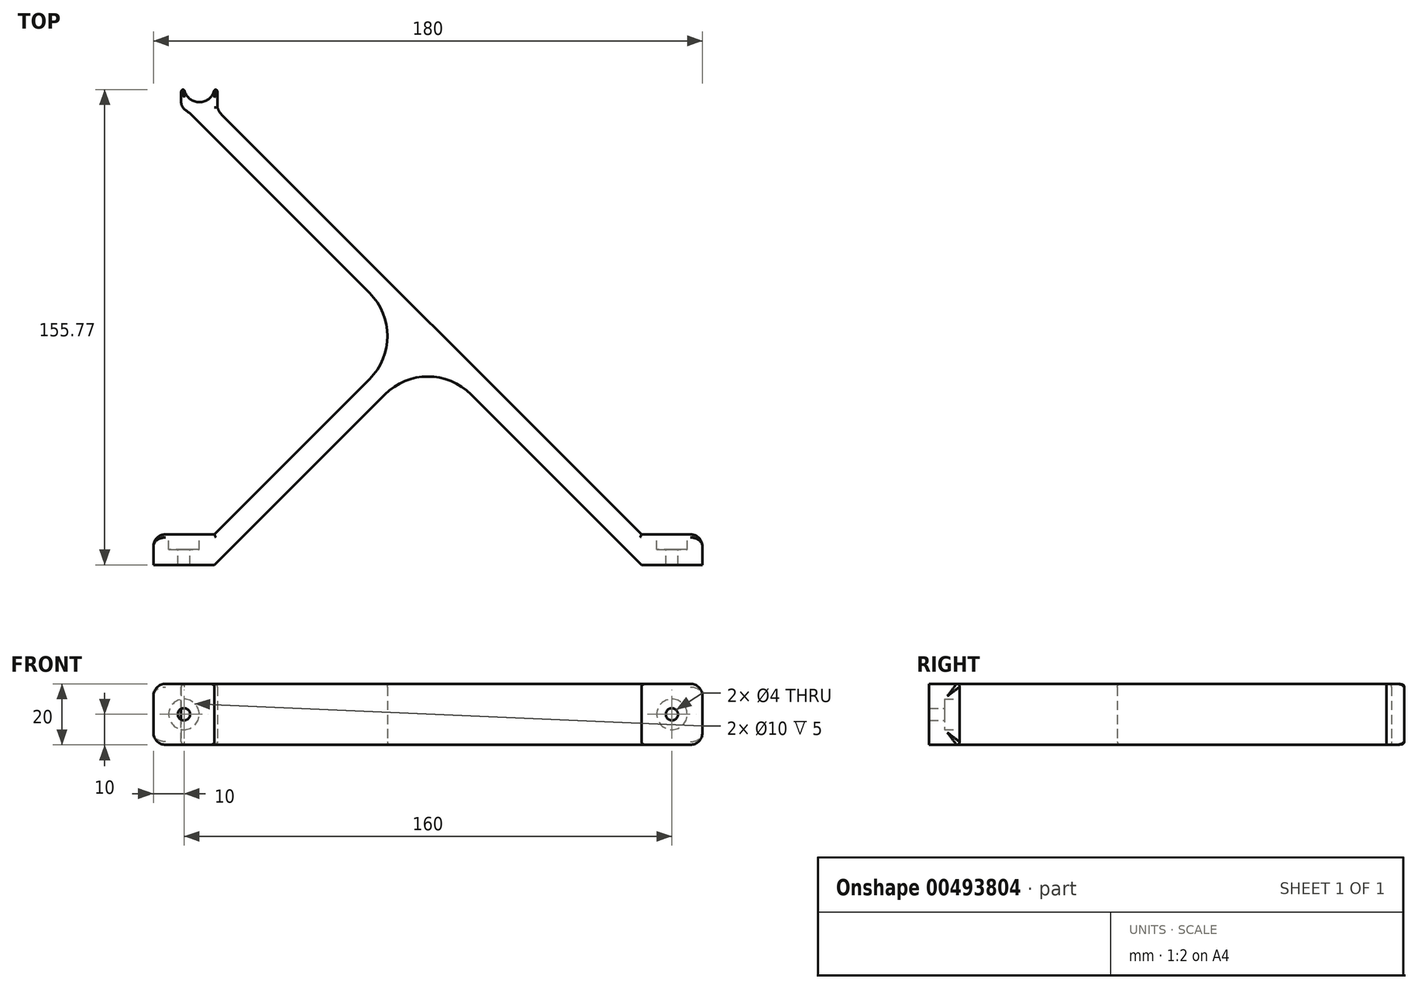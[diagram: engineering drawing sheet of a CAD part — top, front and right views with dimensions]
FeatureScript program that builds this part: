
annotation { "Feature Type Name" : "Feature", "Feature Type Description" : "" }
export const myFeature = defineFeature(function(context is Context, id is Id, definition is map)
    precondition{}
    {
        {
            var Q0;
            Q0=qCreatedBy(makeId("Top.planeOp"),FACE);
            var sketch = newSketch(context, id + "F0", { "sketchPlane" : qUnion([Q0])});
            skLineSegment(sketch, "E0", {"start": v(0, 0) * mm, "end": v(0, -75) * mm, "construction": true});
            skLineSegment(sketch, "E1", {"start": v(0, -75) * mm, "end": v(75, -75) * mm, "construction": true});
            skLineSegment(sketch, "E2", {"start": v(75, -75) * mm, "end": v(-74.9, 74.9) * mm});
            skLineSegment(sketch, "E3", {"start": v(0, 0) * mm, "end": v(-75, -75) * mm});
            skLineSegment(sketch, "E4", {"start": v(-147, -24.26) * mm, "end": v(-137, -24.26) * mm});
            skPoint(sketch, "E5", {"position": v(-142, -24.26) * mm});
            skLineSegment(sketch, "E6", {"start": v(-80, -75) * mm, "end": v(-70, -75) * mm});
            skPoint(sketch, "E7", {"position": v(-75, -75) * mm});
            skLineSegment(sketch, "E8", {"start": v(70, -75) * mm, "end": v(80, -75) * mm});
            skPoint(sketch, "E9", {"position": v(75, -75) * mm});
            skLineSegment(sketch, "E10", {"start": v(-5, -5) * mm, "end": v(5, -5) * mm});
            skPoint(sketch, "E11", {"position": v(0, -5) * mm});
            skLineSegment(sketch, "E12", {"start": v(-70, -75) * mm, "end": v(0, -5) * mm});
            skLineSegment(sketch, "E13", {"start": v(0, -5) * mm, "end": v(70, -75) * mm});
            skLineSegment(sketch, "E14", {"start": v(-5, 5) * mm, "end": v(-5, -5) * mm});
            skPoint(sketch, "E15", {"position": v(-5, 0) * mm});
            skLineSegment(sketch, "E16", {"start": v(-80, -75) * mm, "end": v(-5, 0) * mm});
            skLineSegment(sketch, "E17", {"start": v(80, -75) * mm, "end": v(-70, 75) * mm});
            skLineSegment(sketch, "E18", {"start": v(-70, 75) * mm, "end": v(-74.9, 74.9) * mm});
            skLineSegment(sketch, "E19", {"start": v(-74.9, 74.9) * mm, "end": v(-79.9, 74.9) * mm});
            skLineSegment(sketch, "E20", {"start": v(-79.9, 74.9) * mm, "end": v(-5, 0) * mm});
            skLineSegment(sketch, "E21", {"start": v(-5, 0) * mm, "end": v(-19.14, 14.14) * mm, "construction": true});
            skLineSegment(sketch, "E22", {"start": v(-5, 0) * mm, "end": v(-19.14, -14.14) * mm, "construction": true});
            skArc(sketch, "E23", {"start": v(-19.14, -14.14) * mm, "mid": v(-13.28, 0) * mm, "end": v(-19.14, 14.14) * mm});
            skLineSegment(sketch, "E24", {"start": v(0, -5) * mm, "end": v(-14.14, -19.14) * mm, "construction": true});
            skLineSegment(sketch, "E25", {"start": v(0, -5) * mm, "end": v(14.14, -19.14) * mm, "construction": true});
            skArc(sketch, "E26", {"start": v(14.14, -19.14) * mm, "mid": v(0, -13.28) * mm, "end": v(-14.14, -19.14) * mm});
            skLineSegment(sketch, "E27.bottom", {"start": v(-70, -75) * mm, "end": v(-90, -75) * mm});
            skLineSegment(sketch, "E27.top", {"start": v(-70, -65) * mm, "end": v(-90, -65) * mm});
            skLineSegment(sketch, "E27.left", {"start": v(-70, -75) * mm, "end": v(-70, -65) * mm});
            skLineSegment(sketch, "E27.right", {"start": v(-90, -75) * mm, "end": v(-90, -65) * mm});
            skLineSegment(sketch, "E28.bottom", {"start": v(70, -75) * mm, "end": v(90, -75) * mm});
            skLineSegment(sketch, "E28.top", {"start": v(70, -65) * mm, "end": v(90, -65) * mm});
            skLineSegment(sketch, "E28.left", {"start": v(70, -75) * mm, "end": v(70, -65) * mm});
            skLineSegment(sketch, "E28.right", {"start": v(90, -75) * mm, "end": v(90, -65) * mm});
            skArc(sketch, "E29", {"start": v(-79.9, 80.98) * mm, "mid": v(-74.95, 76.66) * mm, "end": v(-70, 80.98) * mm});
            skLineSegment(sketch, "E30", {"start": v(-79.9, 80.98) * mm, "end": v(-79.9, 74.9) * mm});
            skLineSegment(sketch, "E31", {"start": v(-70, 80.98) * mm, "end": v(-70, 75) * mm});
            skLineSegment(sketch, "E32", {"start": v(-79.9, 74.9) * mm, "end": v(-80.9, 74.9) * mm});
            skLineSegment(sketch, "E33", {"start": v(-80.9, 74.9) * mm, "end": v(-80.9, 80.98) * mm});
            skLineSegment(sketch, "E34", {"start": v(-79.9, 80.98) * mm, "end": v(-80.9, 80.98) * mm});
            skLineSegment(sketch, "E35", {"start": v(-70, 75) * mm, "end": v(-69, 75) * mm});
            skLineSegment(sketch, "E36", {"start": v(-69, 75) * mm, "end": v(-69, 80.98) * mm});
            skLineSegment(sketch, "E37", {"start": v(-69, 80.98) * mm, "end": v(-70, 80.98) * mm});
            skSolve(sketch);
        }
        {
            var Q0;
            {var subQ5=sQuery(id+"F0.wireOp",EDGE,"E12");Q0=makeQuery(id+"F0.imprint","IMPRINT",FACE,{"disambiguationData":[TD([[makeQuery(id+"F0.imprint","IMPRINT",EDGE,{"derivedFrom":subQ5}),1.0]])]});}
            var Q1;
            {var subQ5=sQuery(id+"F0.wireOp",EDGE,"E16");Q1=makeQuery(id+"F0.imprint","IMPRINT",FACE,{"disambiguationData":[TD([[makeQuery(id+"F0.imprint","IMPRINT",EDGE,{"derivedFrom":subQ5}),-1.0]])]});}
            var Q2;
            {var subQ5=sQuery(id+"F0.wireOp",EDGE,"E13");Q2=makeQuery(id+"F0.imprint","IMPRINT",FACE,{"disambiguationData":[TD([[makeQuery(id+"F0.imprint","IMPRINT",EDGE,{"derivedFrom":subQ5}),1.0]])]});}
            var Q3;
            {var subQ7=sQuery(id+"F0.wireOp",EDGE,"E17");Q3=makeQuery(id+"F0.imprint","IMPRINT",FACE,{"disambiguationData":[TD([[makeQuery(id+"F0.imprint","IMPRINT",EDGE,{"derivedFrom":subQ7}),1.0]])]});}
            var Q4;
            {var subQ0=sQuery(id+"F0.wireOp",EDGE,"E19");Q4=makeQuery(id+"F0.imprint","IMPRINT",FACE,{"disambiguationData":[TD([[makeQuery(id+"F0.imprint","IMPRINT",EDGE,{"derivedFrom":subQ0}),1.0]])]});}
            var Q5;
            {var subQ0=sQuery(id+"F0.wireOp",EDGE,"E3");var subQ1=sQuery(id+"F0.wireOp",EDGE,"E2");var subQ2=makeQuery(id+"F0.imprint","INTERSECT",VERTEX,{"derivedFrom":[subQ1,subQ0]});Q5=makeQuery(id+"F0.imprint","IMPRINT",FACE,{"disambiguationData":[TD([[makeQuery(id+"F0.imprint","IMPRINT",EDGE,{"disambiguationData":[TD([[subQ2,-1.0]])],"derivedFrom":subQ1}),1.0]])]});}
            var Q6;
            {var subQ0=sQuery(id+"F0.wireOp",EDGE,"E3");var subQ1=sQuery(id+"F0.wireOp",EDGE,"E2");var subQ2=makeQuery(id+"F0.imprint","INTERSECT",VERTEX,{"derivedFrom":[subQ1,subQ0]});Q6=makeQuery(id+"F0.imprint","IMPRINT",FACE,{"disambiguationData":[TD([[makeQuery(id+"F0.imprint","IMPRINT",EDGE,{"disambiguationData":[TD([[subQ2,1.0]])],"derivedFrom":subQ1}),1.0]])]});}
            var Q7;
            {var subQ3=sQuery(id+"F0.wireOp",EDGE,"E26");Q7=makeQuery(id+"F0.imprint","IMPRINT",FACE,{"disambiguationData":[TD([[makeQuery(id+"F0.imprint","IMPRINT",EDGE,{"derivedFrom":subQ3}),-1.0]])]});}
            var Q8;
            {var subQ3=sQuery(id+"F0.wireOp",EDGE,"E23");Q8=makeQuery(id+"F0.imprint","IMPRINT",FACE,{"disambiguationData":[TD([[makeQuery(id+"F0.imprint","IMPRINT",EDGE,{"derivedFrom":subQ3}),-1.0]])]});}
            var Q9;
            {var subQ3=sQuery(id+"F0.wireOp",EDGE,"E28.top");Q9=makeQuery(id+"F0.imprint","IMPRINT",FACE,{"disambiguationData":[TD([[makeQuery(id+"F0.imprint","IMPRINT",EDGE,{"derivedFrom":subQ3}),-1.0]])]});}
            var Q10;
            {var subQ0=sQuery(id+"F0.wireOp",EDGE,"E28.bottom");var subQ1=sQuery(id+"F0.wireOp",EDGE,"E2");var subQ2=makeQuery(id+"F0.imprint","INTERSECT",VERTEX,{"derivedFrom":[subQ1,subQ0]});Q10=makeQuery(id+"F0.imprint","IMPRINT",FACE,{"disambiguationData":[TD([[makeQuery(id+"F0.imprint","IMPRINT",EDGE,{"disambiguationData":[TD([[subQ2,-1.0]])],"derivedFrom":subQ1}),1.0]])]});}
            var Q11;
            {var subQ0=sQuery(id+"F0.wireOp",EDGE,"E18");Q11=makeQuery(id+"F0.imprint","IMPRINT",FACE,{"disambiguationData":[TD([[makeQuery(id+"F0.imprint","IMPRINT",EDGE,{"derivedFrom":subQ0}),1.0]])]});}
            var Q12;
            {var subQ0=sQuery(id+"F0.wireOp",EDGE,"E27.bottom");var subQ1=sQuery(id+"F0.wireOp",EDGE,"E3");var subQ2=makeQuery(id+"F0.imprint","INTERSECT",VERTEX,{"derivedFrom":[subQ1,subQ0]});Q12=makeQuery(id+"F0.imprint","IMPRINT",FACE,{"disambiguationData":[TD([[makeQuery(id+"F0.imprint","IMPRINT",EDGE,{"disambiguationData":[TD([[subQ2,1.0]])],"derivedFrom":subQ1}),-1.0]])]});}
            var Q13;
            {var subQ0=sQuery(id+"F0.wireOp",EDGE,"E27.bottom");var subQ1=sQuery(id+"F0.wireOp",EDGE,"E3");var subQ2=makeQuery(id+"F0.imprint","INTERSECT",VERTEX,{"derivedFrom":[subQ1,subQ0]});Q13=makeQuery(id+"F0.imprint","IMPRINT",FACE,{"disambiguationData":[TD([[makeQuery(id+"F0.imprint","IMPRINT",EDGE,{"disambiguationData":[TD([[subQ2,1.0]])],"derivedFrom":subQ1}),1.0]])]});}
            var Q14;
            {var subQ3=sQuery(id+"F0.wireOp",EDGE,"E27.top");Q14=makeQuery(id+"F0.imprint","IMPRINT",FACE,{"disambiguationData":[TD([[makeQuery(id+"F0.imprint","IMPRINT",EDGE,{"derivedFrom":subQ3}),1.0]])]});}
            var Q15;
            Q15=makeQuery(id+"F0.imprint","IMPRINT",FACE,{"disambiguationData":[TD([[makeQuery(id+"F0.imprint","IMPRINT",EDGE,{"derivedFrom":sQuery(id+"F0.wireOp",EDGE,"E18")}),-1.0]])]});
            var Q16;
            Q16=makeQuery(id+"F0.imprint","IMPRINT",FACE,{"disambiguationData":[TD([[makeQuery(id+"F0.imprint","IMPRINT",EDGE,{"derivedFrom":sQuery(id+"F0.wireOp",EDGE,"E30")}),-1.0]])]});
            var Q17;
            Q17=makeQuery(id+"F0.imprint","IMPRINT",FACE,{"disambiguationData":[TD([[makeQuery(id+"F0.imprint","IMPRINT",EDGE,{"derivedFrom":sQuery(id+"F0.wireOp",EDGE,"E31")}),1.0]])]});
            extrude(context, id + "F1", {"entities" : qUnion([Q0, Q1, Q2, Q3, Q4, Q5, Q6, Q7, Q8, Q9, Q10, Q11, Q12, Q13, Q14, Q15, Q16, Q17]), "endBound" : BoundingType.SYMMETRIC, "depth" : 20 * mm});
        }
        {
            var Q0;
            Q0=makeQuery(id+"F1.opExtrude","SWEPT_EDGE",EDGE,{"disambiguationData":[OSD([sQuery(id+"F0.wireOp",EDGE,"E19"),sQuery(id+"F0.wireOp",EDGE,"E20"),sQuery(id+"F0.wireOp",EDGE,"E30"),sQuery(id+"F0.wireOp",EDGE,"E32")])]});
            fillet(context, id + "F2", {"entities" : qUnion([Q0]), "radius" : 15 * mm, "tangentPropagation" : true, "allowEdgeOverflow" : false});
        }
        {
            var Q0;
            Q0=makeQuery(id+"F1.opExtrude","SWEPT_EDGE",EDGE,{"disambiguationData":[OSD([sQuery(id+"F0.wireOp",EDGE,"E17"),sQuery(id+"F0.wireOp",EDGE,"E18"),sQuery(id+"F0.wireOp",EDGE,"E31"),sQuery(id+"F0.wireOp",EDGE,"E35")])]});
            fillet(context, id + "F3", {"entities" : qUnion([Q0]), "radius" : 5 * mm, "tangentPropagation" : true, "allowEdgeOverflow" : false});
        }
        {
            var Q0;
            Q0=makeQuery(id+"F2.opFillet","BLEND_EDGE",EDGE,{"blendedFrom":[makeQuery(id+"F1.opExtrude","SWEPT_EDGE",EDGE,{"disambiguationData":[OSD([sQuery(id+"F0.wireOp",EDGE,"E19"),sQuery(id+"F0.wireOp",EDGE,"E20"),sQuery(id+"F0.wireOp",EDGE,"E30"),sQuery(id+"F0.wireOp",EDGE,"E32")])]}),makeQuery(id+"F1.opExtrude","SWEPT_FACE",FACE,{"disambiguationData":[OSD([sQuery(id+"F0.wireOp",EDGE,"E33")])]})],"blendedInto":[makeQuery(id+"F1.opExtrude","SWEPT_FACE",FACE,{"disambiguationData":[OSD([sQuery(id+"F0.wireOp",EDGE,"E33")])]})]});
            fillet(context, id + "F4", {"entities" : qUnion([Q0]), "radius" : 3 * mm, "tangentPropagation" : true, "allowEdgeOverflow" : false});
        }
        {
            var Q0;
            Q0=makeQuery(id+"F1.opExtrude","SWEPT_FACE",FACE,{"disambiguationData":[OSD([sQuery(id+"F0.wireOp",EDGE,"E27.top")])]});
            var sketch = newSketch(context, id + "F5", { "sketchPlane" : qUnion([Q0])});
            skPoint(sketch, "E38", {"position": v(80, 0) * mm});
            skPoint(sketch, "E38.positionSnap0", {"position": v(80, -10) * mm});
            skPoint(sketch, "E38.positionSnap1", {"position": v(90, 0) * mm});
            skCircle(sketch, "E39", {"center": v(80, 0) * mm, "radius": 5 * mm});
            skCircle(sketch, "E40", {"center": v(80, 0) * mm, "radius": 2 * mm});
            skSolve(sketch);
        }
        {
            var Q0;
            Q0=makeQuery(id+"F1.opExtrude","SWEPT_FACE",FACE,{"disambiguationData":[OSD([sQuery(id+"F0.wireOp",EDGE,"E28.top")])]});
            var sketch = newSketch(context, id + "F6", { "sketchPlane" : qUnion([Q0])});
            skPoint(sketch, "E41", {"position": v(-80, 0) * mm});
            skPoint(sketch, "E41.positionSnap0", {"position": v(-80, 10) * mm});
            skPoint(sketch, "E41.positionSnap1", {"position": v(-70, 0) * mm});
            skPoint(sketch, "E42.positionSnap0", {"position": v(-80, -8.37) * mm});
            skPoint(sketch, "E42.positionSnap1", {"position": v(-77.63, 0) * mm});
            skCircle(sketch, "E43", {"center": v(-80, 0) * mm, "radius": 5 * mm});
            skCircle(sketch, "E44", {"center": v(-80, 0) * mm, "radius": 2 * mm});
            skSolve(sketch);
        }
        {
            var Q0;
            Q0=makeQuery(id+"F5.imprint","IMPRINT",FACE,{"disambiguationData":[TD([[makeQuery(id+"F5.imprint","IMPRINT",EDGE,{"derivedFrom":sQuery(id+"F5.wireOp",EDGE,"E40")}),1.0]])]});
            var Q1;
            Q1=makeQuery(id+"F6.imprint","IMPRINT",FACE,{"disambiguationData":[TD([[makeQuery(id+"F6.imprint","IMPRINT",EDGE,{"derivedFrom":sQuery(id+"F6.wireOp",EDGE,"E44")}),1.0]])]});
            extrude(context, id + "F7", {"entities" : qUnion([Q0, Q1]), "operationType" : NewBodyOperationType.REMOVE, "oppositeDirection" : true, "depth" : 25 * mm});
        }
        {
            var Q0;
            Q0=makeQuery(id+"F5.imprint","IMPRINT",FACE,{"disambiguationData":[TD([[makeQuery(id+"F5.imprint","IMPRINT",EDGE,{"derivedFrom":sQuery(id+"F5.wireOp",EDGE,"E39")}),1.0]])]});
            var Q1;
            Q1 = qSketchRegion(id + "F6", true);
            extrude(context, id + "F8", {"entities" : qUnion([Q0, Q1]), "operationType" : NewBodyOperationType.REMOVE, "oppositeDirection" : true, "depth" : 5 * mm});
        }
        {
            var Q0;
            Q0=makeQuery(id+"F1.opExtrude","SWEPT_EDGE",EDGE,{"disambiguationData":[OSD([sQuery(id+"F0.wireOp",EDGE,"E27.top"),sQuery(id+"F0.wireOp",EDGE,"E27.right")])]});
            var Q1;
            Q1=makeQuery(id+"F1.opExtrude","CAP_EDGE",EDGE,{"disambiguationData":[OSD([sQuery(id+"F0.wireOp",EDGE,"E27.right")])],"isStart":false});
            var Q2;
            Q2=makeQuery(id+"F1.opExtrude","CAP_EDGE",EDGE,{"disambiguationData":[OSD([sQuery(id+"F0.wireOp",EDGE,"E27.right")])],"isStart":true});
            var Q3;
            Q3=makeQuery(id+"F1.opExtrude","CAP_EDGE",EDGE,{"disambiguationData":[OSD([sQuery(id+"F0.wireOp",EDGE,"E28.right")])],"isStart":false});
            var Q4;
            Q4=makeQuery(id+"F1.opExtrude","CAP_EDGE",EDGE,{"disambiguationData":[OSD([sQuery(id+"F0.wireOp",EDGE,"E28.right")])],"isStart":true});
            var Q5;
            Q5=makeQuery(id+"F1.opExtrude","SWEPT_EDGE",EDGE,{"disambiguationData":[OSD([sQuery(id+"F0.wireOp",EDGE,"E28.top"),sQuery(id+"F0.wireOp",EDGE,"E28.right")])]});
            fillet(context, id + "F9", {"entities" : qUnion([Q0, Q1, Q2, Q3, Q4, Q5]), "radius" : 4 * mm, "tangentPropagation" : true, "allowEdgeOverflow" : false});
        }
        {
            var Q0;
            Q0=makeQuery(id+"F1.opExtrude","CAP_EDGE",EDGE,{"disambiguationData":[OSD([sQuery(id+"F0.wireOp",EDGE,"E28.top")])],"isStart":true});
            var Q1;
            Q1=makeQuery(id+"F1.opExtrude","CAP_EDGE",EDGE,{"disambiguationData":[OSD([sQuery(id+"F0.wireOp",EDGE,"E28.top")])],"isStart":false});
            var Q2;
            Q2=makeQuery(id+"F1.opExtrude","CAP_EDGE",EDGE,{"disambiguationData":[OSD([sQuery(id+"F0.wireOp",EDGE,"E17")])],"isStart":true});
            var Q3;
            Q3=makeQuery(id+"F1.opExtrude","CAP_EDGE",EDGE,{"disambiguationData":[OSD([sQuery(id+"F0.wireOp",EDGE,"E17")])],"isStart":false});
            var Q4;
            Q4=makeQuery(id+"F1.opExtrude","CAP_EDGE",EDGE,{"disambiguationData":[OSD([sQuery(id+"F0.wireOp",EDGE,"E27.top")])],"isStart":true});
            var Q5;
            Q5=makeQuery(id+"F1.opExtrude","CAP_EDGE",EDGE,{"disambiguationData":[OSD([sQuery(id+"F0.wireOp",EDGE,"E27.top")])],"isStart":false});
            var Q6;
            Q6=makeQuery(id+"F1.opExtrude","CAP_EDGE",EDGE,{"disambiguationData":[OSD([sQuery(id+"F0.wireOp",EDGE,"E13")])],"isStart":true});
            var Q7;
            Q7=makeQuery(id+"F1.opExtrude","CAP_EDGE",EDGE,{"disambiguationData":[OSD([sQuery(id+"F0.wireOp",EDGE,"E13")])],"isStart":false});
            fillet(context, id + "F10", {"entities" : qUnion([Q0, Q1, Q2, Q3, Q4, Q5, Q6, Q7]), "radius" : 1 * mm, "tangentPropagation" : true, "allowEdgeOverflow" : false});
        }
        {
            var Q0;
            Q0=makeQuery(id+"F1.opExtrude","SWEPT_EDGE",EDGE,{"disambiguationData":[OSD([sQuery(id+"F0.wireOp",EDGE,"E29"),sQuery(id+"F0.wireOp",EDGE,"E31"),sQuery(id+"F0.wireOp",EDGE,"E37")])]});
            var Q1;
            Q1=makeQuery(id+"F1.opExtrude","SWEPT_EDGE",EDGE,{"disambiguationData":[OSD([sQuery(id+"F0.wireOp",EDGE,"E36"),sQuery(id+"F0.wireOp",EDGE,"E37")])]});
            var Q2;
            Q2=makeQuery(id+"F1.opExtrude","SWEPT_EDGE",EDGE,{"disambiguationData":[OSD([sQuery(id+"F0.wireOp",EDGE,"E29"),sQuery(id+"F0.wireOp",EDGE,"E30"),sQuery(id+"F0.wireOp",EDGE,"E34")])]});
            var Q3;
            Q3=makeQuery(id+"F1.opExtrude","SWEPT_EDGE",EDGE,{"disambiguationData":[OSD([sQuery(id+"F0.wireOp",EDGE,"E33"),sQuery(id+"F0.wireOp",EDGE,"E34")])]});
            fillet(context, id + "F11", {"entities" : qUnion([Q0, Q1, Q2, Q3]), "radius" : 1 * mm, "tangentPropagation" : true, "allowEdgeOverflow" : false});
        }
        {
            var Q0;
            {var subQ0=sQuery(id+"F0.wireOp",EDGE,"E37");Q0=makeQuery(id+"F11.opFillet","BLEND_EDGE",EDGE,{"blendedFrom":[makeQuery(id+"F1.opExtrude","SWEPT_EDGE",EDGE,{"disambiguationData":[OSD([sQuery(id+"F0.wireOp",EDGE,"E29"),sQuery(id+"F0.wireOp",EDGE,"E31"),subQ0])]}),makeQuery(id+"F1.opExtrude","SWEPT_EDGE",EDGE,{"disambiguationData":[OSD([sQuery(id+"F0.wireOp",EDGE,"E36"),subQ0])]})],"blendedInto":[]});}
            var Q1;
            {var subQ0=sQuery(id+"F0.wireOp",EDGE,"E34");Q1=makeQuery(id+"F11.opFillet","BLEND_EDGE",EDGE,{"blendedFrom":[makeQuery(id+"F1.opExtrude","SWEPT_EDGE",EDGE,{"disambiguationData":[OSD([sQuery(id+"F0.wireOp",EDGE,"E29"),sQuery(id+"F0.wireOp",EDGE,"E30"),subQ0])]}),makeQuery(id+"F1.opExtrude","SWEPT_EDGE",EDGE,{"disambiguationData":[OSD([sQuery(id+"F0.wireOp",EDGE,"E33"),subQ0])]})],"blendedInto":[]});}
            fillet(context, id + "F12", {"entities" : qUnion([Q0, Q1]), "radius" : .5 * mm, "tangentPropagation" : true, "allowEdgeOverflow" : false});
        }
        {
            var Q0;
            Q0=makeQuery(id+"F1.opExtrude","CAP_EDGE",EDGE,{"disambiguationData":[OSD([sQuery(id+"F0.wireOp",EDGE,"E36")])],"isStart":true});
            var Q1;
            Q1=makeQuery(id+"F1.opExtrude","CAP_EDGE",EDGE,{"disambiguationData":[OSD([sQuery(id+"F0.wireOp",EDGE,"E36")])],"isStart":false});
            var Q2;
            Q2=makeQuery(id+"F1.opExtrude","CAP_EDGE",EDGE,{"disambiguationData":[OSD([sQuery(id+"F0.wireOp",EDGE,"E33")])],"isStart":true});
            var Q3;
            {var subQ0=sQuery(id+"F0.wireOp",EDGE,"E33");var subQ1=sQuery(id+"F0.wireOp",EDGE,"E32");var subQ2=sQuery(id+"F0.wireOp",EDGE,"E20");Q3=makeQuery(id+"F4.opFillet","BLEND_EDGE",EDGE,{"blendedFrom":[makeQuery(id+"F2.opFillet","BLEND_EDGE",EDGE,{"blendedFrom":[makeQuery(id+"F1.opExtrude","SWEPT_EDGE",EDGE,{"disambiguationData":[OSD([sQuery(id+"F0.wireOp",EDGE,"E19"),subQ2,sQuery(id+"F0.wireOp",EDGE,"E30"),subQ1])]}),makeQuery(id+"F1.opExtrude","SWEPT_FACE",FACE,{"disambiguationData":[OSD([subQ0])]})],"blendedInto":[makeQuery(id+"F1.opExtrude","SWEPT_FACE",FACE,{"disambiguationData":[OSD([subQ0])]})]}),makeQuery(id+"F1.opExtrude","CAP_FACE",FACE,{"disambiguationData":[OSD([sQuery(id+"F0.wireOp",EDGE,"E12"),sQuery(id+"F0.wireOp",EDGE,"E13"),sQuery(id+"F0.wireOp",EDGE,"E16"),sQuery(id+"F0.wireOp",EDGE,"E17"),subQ2,sQuery(id+"F0.wireOp",EDGE,"E23"),sQuery(id+"F0.wireOp",EDGE,"E26"),sQuery(id+"F0.wireOp",EDGE,"E27.bottom"),sQuery(id+"F0.wireOp",EDGE,"E27.top"),sQuery(id+"F0.wireOp",EDGE,"E27.right"),sQuery(id+"F0.wireOp",EDGE,"E28.bottom"),sQuery(id+"F0.wireOp",EDGE,"E28.top"),sQuery(id+"F0.wireOp",EDGE,"E28.right"),sQuery(id+"F0.wireOp",EDGE,"E29"),subQ1,subQ0,sQuery(id+"F0.wireOp",EDGE,"E34"),sQuery(id+"F0.wireOp",EDGE,"E35"),sQuery(id+"F0.wireOp",EDGE,"E36"),sQuery(id+"F0.wireOp",EDGE,"E37")])],"isStart":true})],"blendedInto":[makeQuery(id+"F1.opExtrude","CAP_FACE",FACE,{"disambiguationData":[OSD([sQuery(id+"F0.wireOp",EDGE,"E12"),sQuery(id+"F0.wireOp",EDGE,"E13"),sQuery(id+"F0.wireOp",EDGE,"E16"),sQuery(id+"F0.wireOp",EDGE,"E17"),subQ2,sQuery(id+"F0.wireOp",EDGE,"E23"),sQuery(id+"F0.wireOp",EDGE,"E26"),sQuery(id+"F0.wireOp",EDGE,"E27.bottom"),sQuery(id+"F0.wireOp",EDGE,"E27.top"),sQuery(id+"F0.wireOp",EDGE,"E27.right"),sQuery(id+"F0.wireOp",EDGE,"E28.bottom"),sQuery(id+"F0.wireOp",EDGE,"E28.top"),sQuery(id+"F0.wireOp",EDGE,"E28.right"),sQuery(id+"F0.wireOp",EDGE,"E29"),subQ1,subQ0,sQuery(id+"F0.wireOp",EDGE,"E34"),sQuery(id+"F0.wireOp",EDGE,"E35"),sQuery(id+"F0.wireOp",EDGE,"E36"),sQuery(id+"F0.wireOp",EDGE,"E37")])],"isStart":true})]});}
            var Q4;
            Q4=makeQuery(id+"F1.opExtrude","CAP_EDGE",EDGE,{"disambiguationData":[OSD([sQuery(id+"F0.wireOp",EDGE,"E33")])],"isStart":false});
            var Q5;
            {var subQ0=sQuery(id+"F0.wireOp",EDGE,"E33");var subQ1=sQuery(id+"F0.wireOp",EDGE,"E32");var subQ2=sQuery(id+"F0.wireOp",EDGE,"E20");Q5=makeQuery(id+"F4.opFillet","BLEND_EDGE",EDGE,{"blendedFrom":[makeQuery(id+"F2.opFillet","BLEND_EDGE",EDGE,{"blendedFrom":[makeQuery(id+"F1.opExtrude","SWEPT_EDGE",EDGE,{"disambiguationData":[OSD([sQuery(id+"F0.wireOp",EDGE,"E19"),subQ2,sQuery(id+"F0.wireOp",EDGE,"E30"),subQ1])]}),makeQuery(id+"F1.opExtrude","SWEPT_FACE",FACE,{"disambiguationData":[OSD([subQ0])]})],"blendedInto":[makeQuery(id+"F1.opExtrude","SWEPT_FACE",FACE,{"disambiguationData":[OSD([subQ0])]})]}),makeQuery(id+"F1.opExtrude","CAP_FACE",FACE,{"disambiguationData":[OSD([sQuery(id+"F0.wireOp",EDGE,"E12"),sQuery(id+"F0.wireOp",EDGE,"E13"),sQuery(id+"F0.wireOp",EDGE,"E16"),sQuery(id+"F0.wireOp",EDGE,"E17"),subQ2,sQuery(id+"F0.wireOp",EDGE,"E23"),sQuery(id+"F0.wireOp",EDGE,"E26"),sQuery(id+"F0.wireOp",EDGE,"E27.bottom"),sQuery(id+"F0.wireOp",EDGE,"E27.top"),sQuery(id+"F0.wireOp",EDGE,"E27.right"),sQuery(id+"F0.wireOp",EDGE,"E28.bottom"),sQuery(id+"F0.wireOp",EDGE,"E28.top"),sQuery(id+"F0.wireOp",EDGE,"E28.right"),sQuery(id+"F0.wireOp",EDGE,"E29"),subQ1,subQ0,sQuery(id+"F0.wireOp",EDGE,"E34"),sQuery(id+"F0.wireOp",EDGE,"E35"),sQuery(id+"F0.wireOp",EDGE,"E36"),sQuery(id+"F0.wireOp",EDGE,"E37")])],"isStart":false})],"blendedInto":[makeQuery(id+"F1.opExtrude","CAP_FACE",FACE,{"disambiguationData":[OSD([sQuery(id+"F0.wireOp",EDGE,"E12"),sQuery(id+"F0.wireOp",EDGE,"E13"),sQuery(id+"F0.wireOp",EDGE,"E16"),sQuery(id+"F0.wireOp",EDGE,"E17"),subQ2,sQuery(id+"F0.wireOp",EDGE,"E23"),sQuery(id+"F0.wireOp",EDGE,"E26"),sQuery(id+"F0.wireOp",EDGE,"E27.bottom"),sQuery(id+"F0.wireOp",EDGE,"E27.top"),sQuery(id+"F0.wireOp",EDGE,"E27.right"),sQuery(id+"F0.wireOp",EDGE,"E28.bottom"),sQuery(id+"F0.wireOp",EDGE,"E28.top"),sQuery(id+"F0.wireOp",EDGE,"E28.right"),sQuery(id+"F0.wireOp",EDGE,"E29"),subQ1,subQ0,sQuery(id+"F0.wireOp",EDGE,"E34"),sQuery(id+"F0.wireOp",EDGE,"E35"),sQuery(id+"F0.wireOp",EDGE,"E36"),sQuery(id+"F0.wireOp",EDGE,"E37")])],"isStart":false})]});}
            var Q6;
            {var subQ0=sQuery(id+"F0.wireOp",EDGE,"E32");var subQ1=sQuery(id+"F0.wireOp",EDGE,"E20");Q6=makeQuery(id+"F2.opFillet","BLEND_EDGE",EDGE,{"blendedFrom":[makeQuery(id+"F1.opExtrude","SWEPT_EDGE",EDGE,{"disambiguationData":[OSD([sQuery(id+"F0.wireOp",EDGE,"E19"),subQ1,sQuery(id+"F0.wireOp",EDGE,"E30"),subQ0])]}),makeQuery(id+"F1.opExtrude","CAP_FACE",FACE,{"disambiguationData":[OSD([sQuery(id+"F0.wireOp",EDGE,"E12"),sQuery(id+"F0.wireOp",EDGE,"E13"),sQuery(id+"F0.wireOp",EDGE,"E16"),sQuery(id+"F0.wireOp",EDGE,"E17"),subQ1,sQuery(id+"F0.wireOp",EDGE,"E23"),sQuery(id+"F0.wireOp",EDGE,"E26"),sQuery(id+"F0.wireOp",EDGE,"E27.bottom"),sQuery(id+"F0.wireOp",EDGE,"E27.top"),sQuery(id+"F0.wireOp",EDGE,"E27.right"),sQuery(id+"F0.wireOp",EDGE,"E28.bottom"),sQuery(id+"F0.wireOp",EDGE,"E28.top"),sQuery(id+"F0.wireOp",EDGE,"E28.right"),sQuery(id+"F0.wireOp",EDGE,"E29"),subQ0,sQuery(id+"F0.wireOp",EDGE,"E33"),sQuery(id+"F0.wireOp",EDGE,"E34"),sQuery(id+"F0.wireOp",EDGE,"E35"),sQuery(id+"F0.wireOp",EDGE,"E36"),sQuery(id+"F0.wireOp",EDGE,"E37")])],"isStart":false})],"blendedInto":[makeQuery(id+"F1.opExtrude","CAP_FACE",FACE,{"disambiguationData":[OSD([sQuery(id+"F0.wireOp",EDGE,"E12"),sQuery(id+"F0.wireOp",EDGE,"E13"),sQuery(id+"F0.wireOp",EDGE,"E16"),sQuery(id+"F0.wireOp",EDGE,"E17"),subQ1,sQuery(id+"F0.wireOp",EDGE,"E23"),sQuery(id+"F0.wireOp",EDGE,"E26"),sQuery(id+"F0.wireOp",EDGE,"E27.bottom"),sQuery(id+"F0.wireOp",EDGE,"E27.top"),sQuery(id+"F0.wireOp",EDGE,"E27.right"),sQuery(id+"F0.wireOp",EDGE,"E28.bottom"),sQuery(id+"F0.wireOp",EDGE,"E28.top"),sQuery(id+"F0.wireOp",EDGE,"E28.right"),sQuery(id+"F0.wireOp",EDGE,"E29"),subQ0,sQuery(id+"F0.wireOp",EDGE,"E33"),sQuery(id+"F0.wireOp",EDGE,"E34"),sQuery(id+"F0.wireOp",EDGE,"E35"),sQuery(id+"F0.wireOp",EDGE,"E36"),sQuery(id+"F0.wireOp",EDGE,"E37")])],"isStart":false})]});}
            var Q7;
            {var subQ0=sQuery(id+"F0.wireOp",EDGE,"E32");var subQ1=sQuery(id+"F0.wireOp",EDGE,"E20");Q7=makeQuery(id+"F2.opFillet","BLEND_EDGE",EDGE,{"blendedFrom":[makeQuery(id+"F1.opExtrude","SWEPT_EDGE",EDGE,{"disambiguationData":[OSD([sQuery(id+"F0.wireOp",EDGE,"E19"),subQ1,sQuery(id+"F0.wireOp",EDGE,"E30"),subQ0])]}),makeQuery(id+"F1.opExtrude","CAP_FACE",FACE,{"disambiguationData":[OSD([sQuery(id+"F0.wireOp",EDGE,"E12"),sQuery(id+"F0.wireOp",EDGE,"E13"),sQuery(id+"F0.wireOp",EDGE,"E16"),sQuery(id+"F0.wireOp",EDGE,"E17"),subQ1,sQuery(id+"F0.wireOp",EDGE,"E23"),sQuery(id+"F0.wireOp",EDGE,"E26"),sQuery(id+"F0.wireOp",EDGE,"E27.bottom"),sQuery(id+"F0.wireOp",EDGE,"E27.top"),sQuery(id+"F0.wireOp",EDGE,"E27.right"),sQuery(id+"F0.wireOp",EDGE,"E28.bottom"),sQuery(id+"F0.wireOp",EDGE,"E28.top"),sQuery(id+"F0.wireOp",EDGE,"E28.right"),sQuery(id+"F0.wireOp",EDGE,"E29"),subQ0,sQuery(id+"F0.wireOp",EDGE,"E33"),sQuery(id+"F0.wireOp",EDGE,"E34"),sQuery(id+"F0.wireOp",EDGE,"E35"),sQuery(id+"F0.wireOp",EDGE,"E36"),sQuery(id+"F0.wireOp",EDGE,"E37")])],"isStart":true})],"blendedInto":[makeQuery(id+"F1.opExtrude","CAP_FACE",FACE,{"disambiguationData":[OSD([sQuery(id+"F0.wireOp",EDGE,"E12"),sQuery(id+"F0.wireOp",EDGE,"E13"),sQuery(id+"F0.wireOp",EDGE,"E16"),sQuery(id+"F0.wireOp",EDGE,"E17"),subQ1,sQuery(id+"F0.wireOp",EDGE,"E23"),sQuery(id+"F0.wireOp",EDGE,"E26"),sQuery(id+"F0.wireOp",EDGE,"E27.bottom"),sQuery(id+"F0.wireOp",EDGE,"E27.top"),sQuery(id+"F0.wireOp",EDGE,"E27.right"),sQuery(id+"F0.wireOp",EDGE,"E28.bottom"),sQuery(id+"F0.wireOp",EDGE,"E28.top"),sQuery(id+"F0.wireOp",EDGE,"E28.right"),sQuery(id+"F0.wireOp",EDGE,"E29"),subQ0,sQuery(id+"F0.wireOp",EDGE,"E33"),sQuery(id+"F0.wireOp",EDGE,"E34"),sQuery(id+"F0.wireOp",EDGE,"E35"),sQuery(id+"F0.wireOp",EDGE,"E36"),sQuery(id+"F0.wireOp",EDGE,"E37")])],"isStart":true})]});}
            fillet(context, id + "F13", {"entities" : qUnion([Q0, Q1, Q2, Q3, Q4, Q5, Q6, Q7]), "radius" : 1 * mm, "tangentPropagation" : true, "allowEdgeOverflow" : false});
        }
    });
